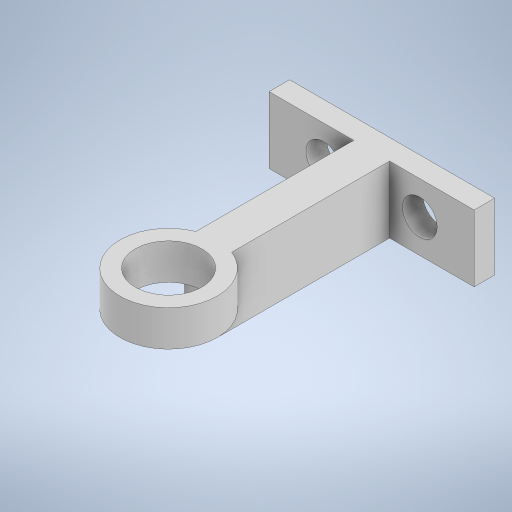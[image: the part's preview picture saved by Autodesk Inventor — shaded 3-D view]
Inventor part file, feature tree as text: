
AUTODESK INVENTOR PART (.ipt)
format: ipt  version: 2023 (Build 270158000, 158)  size: 265,216 bytes
history: native  units: mm
features: extrude x3, sketch x3, other x1, plane x1
ambient origin geometry x8: Origin, YZ Plane, XZ Plane, XY Plane, X Axis, Y Axis, Z Axis, Center Point
bodies: Body1 (feature_tree)
feature tree (8):
  other  "實體1"
  extrude  "擠出1"  Depth=40.0mm
  extrude  "擠出2"  Depth=13.0mm
  plane  "工作平面2"
  extrude  "擠出3"  Depth=6.8mm
  sketch  "草圖1"
  sketch  "草圖3"
  sketch  "草圖4"
